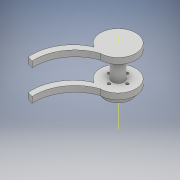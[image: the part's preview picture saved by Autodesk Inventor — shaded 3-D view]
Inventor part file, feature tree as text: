
AUTODESK INVENTOR PART (.ipt)
format: ipt  version: 2017 (Build 210142000, 142)  size: 157,696 bytes
history: native  units: mm
features: extrude x5, sketch x5, pattern_linear x1, projected_geometry x1
ambient origin geometry x8: Origin, YZ Plane, XZ Plane, XY Plane, X Axis, Y Axis, Z Axis, Center Point
bodies: Solide1 (feature_tree)
feature tree (12):
  extrude  "Extrusion1"  Depth=10.0mm TaperAngle=0.0deg
  extrude  "Extrusion3"  Depth=35.0mm
  extrude  "Extrusion4"  Depth=30.0mm
  extrude  "Extrusion5"  Depth=5.0mm TaperAngle=0.0deg
  pattern_linear  "Réseau rectangulaire1"  Spacing1=46.25mm  [1 undecoded]
  extrude  "Extrusion6"  Depth=10.0mm
  sketch  "Esquisse1"
  sketch  "Esquisse3"
  sketch  "Esquisse4"
  projected_geometry  "Boucle projetée2"
  sketch  "Esquisse5"
  sketch  "Esquisse6"
note: 1 required parameter value undecoded (feature->parameter linkage not recoverable at this tier; creation-order binding heuristic only, values carry confidence <= 0.55)
